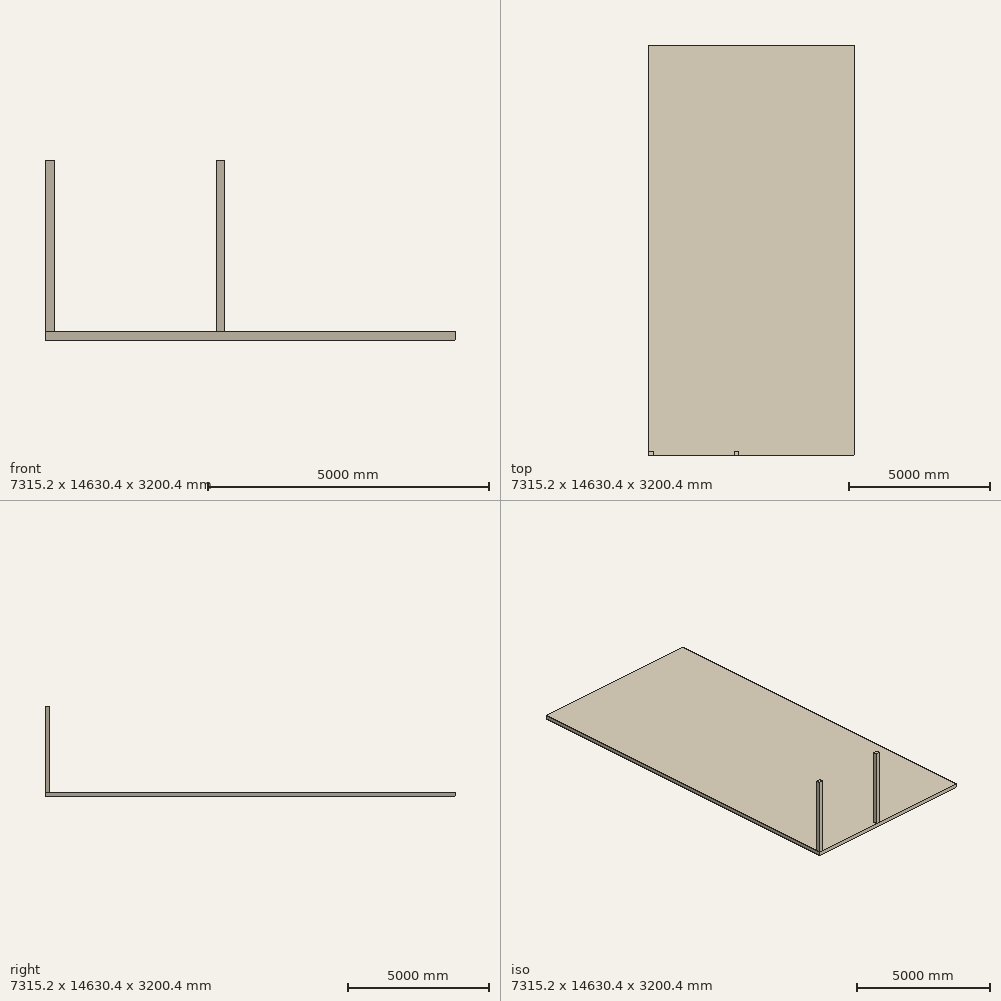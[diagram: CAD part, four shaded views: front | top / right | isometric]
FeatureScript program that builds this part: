
annotation { "Feature Type Name" : "Feature", "Feature Type Description" : "" }
export const myFeature = defineFeature(function(context is Context, id is Id, definition is map)
    precondition{}
    {
        {
            var Q0;
            Q0=qCreatedBy(makeId("Top.planeOp"),FACE);
            var sketch = newSketch(context, id + "F0", { "sketchPlane" : qUnion([Q0])});
            skLineSegment(sketch, "E0.rect.bottom", {"start": v(-3657.6, 7315.2) * mm, "end": v(3657.6, 7315.2) * mm});
            skLineSegment(sketch, "E0.rect.top", {"start": v(-3657.6, -7315.2) * mm, "end": v(3657.6, -7315.2) * mm});
            skLineSegment(sketch, "E0.rect.left", {"start": v(-3657.6, 7315.2) * mm, "end": v(-3657.6, -7315.2) * mm});
            skLineSegment(sketch, "E0.rect.right", {"start": v(3657.6, 7315.2) * mm, "end": v(3657.6, -7315.2) * mm});
            skPoint(sketch, "E0.rect.middle", {"position": v(0, 0) * mm});
            skSolve(sketch);
        }
        {
            var Q0;
            Q0=makeQuery(id+"F0.imprint","IMPRINT",FACE,{"disambiguationData":[TD([[makeQuery(id+"F0.imprint","IMPRINT",EDGE,{"derivedFrom":sQuery(id+"F0.wireOp",EDGE,"E0.rect.bottom")}),-1.0]])]});
            extrude(context, id + "F1", {"entities" : qUnion([Q0]), "depth" : 152.4 * mm});
        }
        {
            var Q0;
            Q0=makeQuery(id+"F1.opExtrude","CAP_FACE",FACE,{"disambiguationData":[OSD([sQuery(id+"F0.wireOp",EDGE,"E0.rect.bottom"),sQuery(id+"F0.wireOp",EDGE,"E0.rect.top"),sQuery(id+"F0.wireOp",EDGE,"E0.rect.left"),sQuery(id+"F0.wireOp",EDGE,"E0.rect.right")])],"isStart":false});
            var sketch = newSketch(context, id + "F2", { "sketchPlane" : qUnion([Q0])});
            skLineSegment(sketch, "E1.bottom", {"start": v(-3657.6, -7315.2) * mm, "end": v(-3505.2, -7315.2) * mm});
            skLineSegment(sketch, "E1.top", {"start": v(-3657.6, -7162.8) * mm, "end": v(-3505.2, -7162.8) * mm});
            skLineSegment(sketch, "E1.left", {"start": v(-3657.6, -7315.2) * mm, "end": v(-3657.6, -7162.8) * mm});
            skLineSegment(sketch, "E1.right", {"start": v(-3505.2, -7315.2) * mm, "end": v(-3505.2, -7162.8) * mm});
            skSolve(sketch);
        }
        {
            var Q0;
            Q0=makeQuery(id+"F2.imprint","IMPRINT",FACE,{"disambiguationData":[TD([[makeQuery(id+"F2.imprint","IMPRINT",EDGE,{"derivedFrom":sQuery(id+"F2.wireOp",EDGE,"E1.bottom")}),1.0]])]});
            extrude(context, id + "F3", {"entities" : qUnion([Q0]), "depth" : 3048 * mm});
        }
        {
            var Q0;
            Q0=makeQuery(id+"F3.opExtrude","SWEPT_BODY",BODY,{"disambiguationData":[OSD([sQuery(id+"F2.wireOp",EDGE,"E1.bottom"),sQuery(id+"F2.wireOp",EDGE,"E1.top"),sQuery(id+"F2.wireOp",EDGE,"E1.left"),sQuery(id+"F2.wireOp",EDGE,"E1.right")])]});
            transform(context, id + "F4", {"entities" : qUnion([Q0]), "transformType" : TransformType.TRANSLATION_3D, "dx" : 0 * mm, "dy" : 0 * mm, "dz" : 0 * mm, "makeCopy" : true});
        }
        {
            var Q0;
            Q0=makeQuery(id+"F4.opPattern","COPY",BODY,{"derivedFrom":makeQuery(id+"F3.opExtrude","SWEPT_BODY",BODY,{"disambiguationData":[OSD([sQuery(id+"F2.wireOp",EDGE,"E1.bottom"),sQuery(id+"F2.wireOp",EDGE,"E1.top"),sQuery(id+"F2.wireOp",EDGE,"E1.left"),sQuery(id+"F2.wireOp",EDGE,"E1.right")])]}),"instanceName":"1"});
            deleteBodies(context, id + "F5", {"entities" : qUnion([Q0])});
        }
        {
            var Q0;
            Q0=makeQuery(id+"F3.opExtrude","SWEPT_BODY",BODY,{"disambiguationData":[OSD([sQuery(id+"F2.wireOp",EDGE,"E1.bottom"),sQuery(id+"F2.wireOp",EDGE,"E1.top"),sQuery(id+"F2.wireOp",EDGE,"E1.left"),sQuery(id+"F2.wireOp",EDGE,"E1.right")])]});
            transform(context, id + "F6", {"entities" : qUnion([Q0]), "transformType" : TransformType.TRANSLATION_3D, "dx" : 0 * mm, "dy" : 0 * mm, "dz" : 0 * mm, "makeCopy" : true});
        }
        {
            var Q0;
            Q0=makeQuery(id+"F3.opExtrude","SWEPT_BODY",BODY,{"disambiguationData":[OSD([sQuery(id+"F2.wireOp",EDGE,"E1.bottom"),sQuery(id+"F2.wireOp",EDGE,"E1.top"),sQuery(id+"F2.wireOp",EDGE,"E1.left"),sQuery(id+"F2.wireOp",EDGE,"E1.right")])]});
            transform(context, id + "F7", {"entities" : qUnion([Q0]), "transformType" : TransformType.TRANSLATION_3D, "dx" : 0 * mm, "dy" : 3048 * mm, "dz" : 0 * mm, "makeCopy" : true});
        }
        {
            var Q0;
            Q0=makeQuery(id+"F6.opPattern","COPY",BODY,{"derivedFrom":makeQuery(id+"F3.opExtrude","SWEPT_BODY",BODY,{"disambiguationData":[OSD([sQuery(id+"F2.wireOp",EDGE,"E1.bottom"),sQuery(id+"F2.wireOp",EDGE,"E1.top"),sQuery(id+"F2.wireOp",EDGE,"E1.left"),sQuery(id+"F2.wireOp",EDGE,"E1.right")])]}),"instanceName":"1"});
            deleteBodies(context, id + "F8", {"entities" : qUnion([Q0])});
        }
        {
            var Q0;
            Q0=makeQuery(id+"F7.opPattern","COPY",BODY,{"derivedFrom":makeQuery(id+"F3.opExtrude","SWEPT_BODY",BODY,{"disambiguationData":[OSD([sQuery(id+"F2.wireOp",EDGE,"E1.bottom"),sQuery(id+"F2.wireOp",EDGE,"E1.top"),sQuery(id+"F2.wireOp",EDGE,"E1.left"),sQuery(id+"F2.wireOp",EDGE,"E1.right")])]}),"instanceName":"1"});
            transform(context, id + "F9", {"entities" : qUnion([Q0]), "transformType" : TransformType.TRANSLATION_3D, "dx" : 0 * mm, "dy" : 2438.4 * mm, "dz" : 0 * mm, "makeCopy" : true});
        }
        {
            var Q0;
            Q0=makeQuery(id+"F9.opPattern","COPY",BODY,{"derivedFrom":makeQuery(id+"F7.opPattern","COPY",BODY,{"derivedFrom":makeQuery(id+"F3.opExtrude","SWEPT_BODY",BODY,{"disambiguationData":[OSD([sQuery(id+"F2.wireOp",EDGE,"E1.bottom"),sQuery(id+"F2.wireOp",EDGE,"E1.top"),sQuery(id+"F2.wireOp",EDGE,"E1.left"),sQuery(id+"F2.wireOp",EDGE,"E1.right")])]}),"instanceName":"1"}),"instanceName":"1"});
            transform(context, id + "F10", {"entities" : qUnion([Q0]), "transformType" : TransformType.TRANSLATION_3D, "dx" : 0 * mm, "dy" : 2438.4 * mm, "dz" : 0 * mm, "makeCopy" : true});
        }
        {
            var Q0;
            Q0=makeQuery(id+"F10.opPattern","COPY",BODY,{"derivedFrom":makeQuery(id+"F9.opPattern","COPY",BODY,{"derivedFrom":makeQuery(id+"F7.opPattern","COPY",BODY,{"derivedFrom":makeQuery(id+"F3.opExtrude","SWEPT_BODY",BODY,{"disambiguationData":[OSD([sQuery(id+"F2.wireOp",EDGE,"E1.bottom"),sQuery(id+"F2.wireOp",EDGE,"E1.top"),sQuery(id+"F2.wireOp",EDGE,"E1.left"),sQuery(id+"F2.wireOp",EDGE,"E1.right")])]}),"instanceName":"1"}),"instanceName":"1"}),"instanceName":"1"});
            var Q1;
            Q1=makeQuery(id+"F9.opPattern","COPY",BODY,{"derivedFrom":makeQuery(id+"F7.opPattern","COPY",BODY,{"derivedFrom":makeQuery(id+"F3.opExtrude","SWEPT_BODY",BODY,{"disambiguationData":[OSD([sQuery(id+"F2.wireOp",EDGE,"E1.bottom"),sQuery(id+"F2.wireOp",EDGE,"E1.top"),sQuery(id+"F2.wireOp",EDGE,"E1.left"),sQuery(id+"F2.wireOp",EDGE,"E1.right")])]}),"instanceName":"1"}),"instanceName":"1"});
            deleteBodies(context, id + "F11", {"entities" : qUnion([Q0, Q1])});
        }
        {
            var Q0;
            Q0=makeQuery(id+"F7.opPattern","COPY",BODY,{"derivedFrom":makeQuery(id+"F3.opExtrude","SWEPT_BODY",BODY,{"disambiguationData":[OSD([sQuery(id+"F2.wireOp",EDGE,"E1.bottom"),sQuery(id+"F2.wireOp",EDGE,"E1.top"),sQuery(id+"F2.wireOp",EDGE,"E1.left"),sQuery(id+"F2.wireOp",EDGE,"E1.right")])]}),"instanceName":"1"});
            transform(context, id + "F12", {"entities" : qUnion([Q0]), "transformType" : TransformType.TRANSLATION_3D, "dx" : 0 * mm, "dy" : 3048 * mm, "dz" : 0 * mm, "makeCopy" : true});
        }
        {
            var Q0;
            Q0=makeQuery(id+"F12.opPattern","COPY",BODY,{"derivedFrom":makeQuery(id+"F7.opPattern","COPY",BODY,{"derivedFrom":makeQuery(id+"F3.opExtrude","SWEPT_BODY",BODY,{"disambiguationData":[OSD([sQuery(id+"F2.wireOp",EDGE,"E1.bottom"),sQuery(id+"F2.wireOp",EDGE,"E1.top"),sQuery(id+"F2.wireOp",EDGE,"E1.left"),sQuery(id+"F2.wireOp",EDGE,"E1.right")])]}),"instanceName":"1"}),"instanceName":"1"});
            var Q1;
            Q1=makeQuery(id+"F7.opPattern","COPY",BODY,{"derivedFrom":makeQuery(id+"F3.opExtrude","SWEPT_BODY",BODY,{"disambiguationData":[OSD([sQuery(id+"F2.wireOp",EDGE,"E1.bottom"),sQuery(id+"F2.wireOp",EDGE,"E1.top"),sQuery(id+"F2.wireOp",EDGE,"E1.left"),sQuery(id+"F2.wireOp",EDGE,"E1.right")])]}),"instanceName":"1"});
            deleteBodies(context, id + "F13", {"entities" : qUnion([Q0, Q1])});
        }
        {
            var Q0;
            Q0=makeQuery(id+"F3.opExtrude","SWEPT_BODY",BODY,{"disambiguationData":[OSD([sQuery(id+"F2.wireOp",EDGE,"E1.bottom"),sQuery(id+"F2.wireOp",EDGE,"E1.top"),sQuery(id+"F2.wireOp",EDGE,"E1.left"),sQuery(id+"F2.wireOp",EDGE,"E1.right")])]});
            transform(context, id + "F14", {"entities" : qUnion([Q0]), "transformType" : TransformType.TRANSLATION_3D, "dx" : 3048 * mm, "dy" : 0 * mm, "dz" : 0 * mm, "makeCopy" : true});
        }
    });
